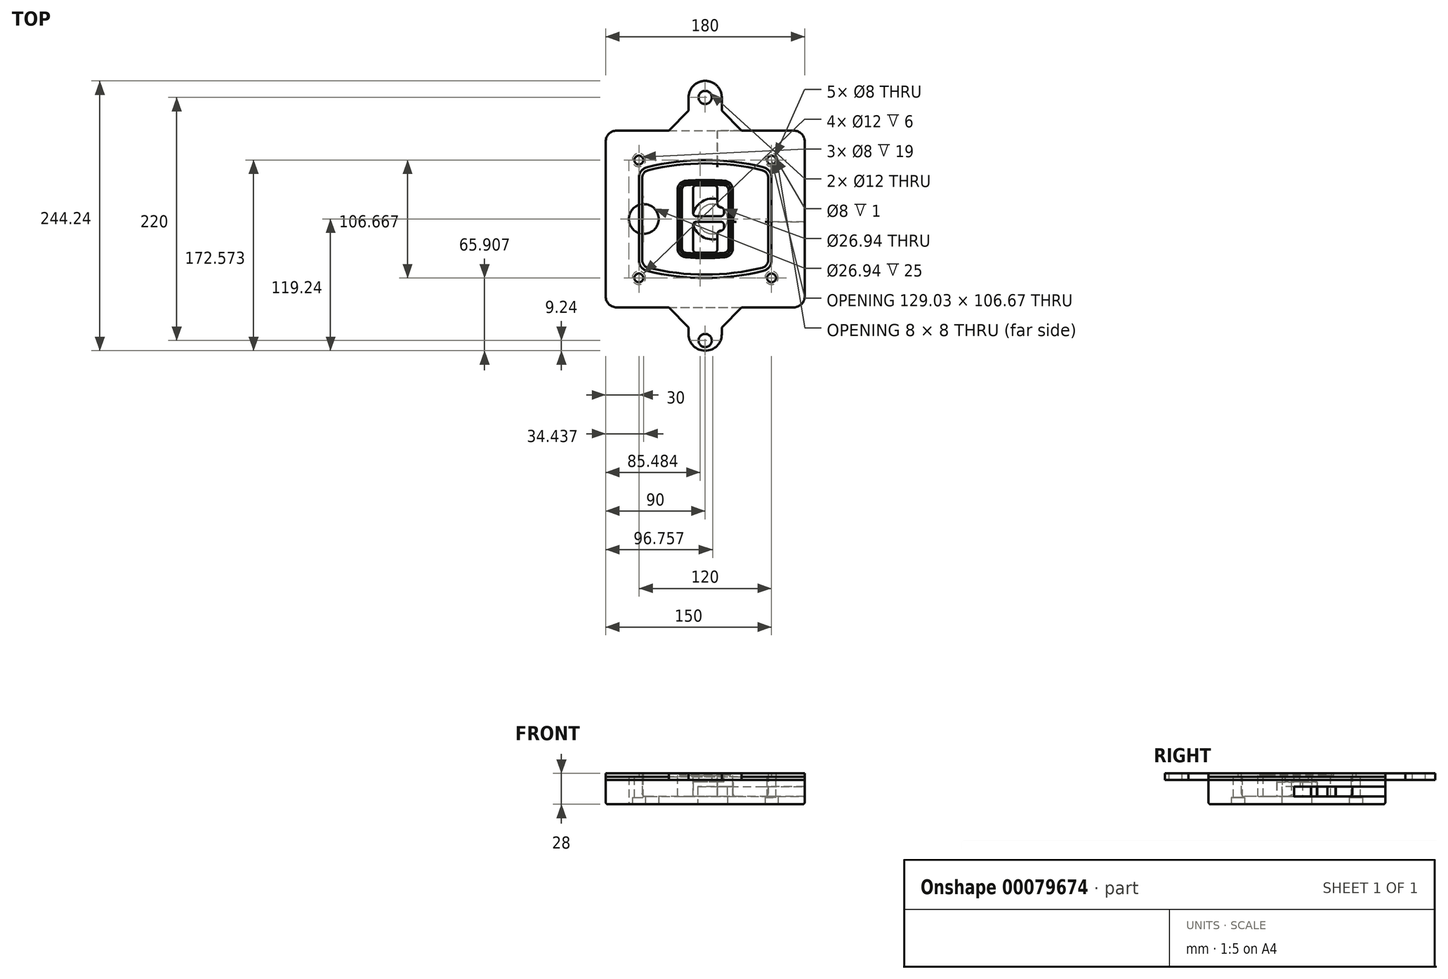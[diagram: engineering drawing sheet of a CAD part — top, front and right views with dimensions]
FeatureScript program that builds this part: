
annotation { "Feature Type Name" : "Feature", "Feature Type Description" : "" }
export const myFeature = defineFeature(function(context is Context, id is Id, definition is map)
    precondition{}
    {
        {
            var Q0;
            Q0=qCreatedBy(makeId("Top.planeOp"),FACE);
            var sketch = newSketch(context, id + "F0", { "sketchPlane" : qUnion([Q0])});
            skPoint(sketch, "E0.rect.middle", {"position": v(0, 0) * mm});
            skLineSegment(sketch, "E1.bottom", {"start": v(-80, -80) * mm, "end": v(80, -80) * mm});
            skLineSegment(sketch, "E1.top", {"start": v(-80, 80) * mm, "end": v(80, 80) * mm});
            skLineSegment(sketch, "E1.left", {"start": v(-90, -70) * mm, "end": v(-90, 70) * mm});
            skLineSegment(sketch, "E1.right", {"start": v(90, -70) * mm, "end": v(90, 70) * mm});
            skLineSegment(sketch, "E2", {"start": v(-90, 80) * mm, "end": v(90, -80) * mm, "construction": true});
            skLineSegment(sketch, "E3", {"start": v(90, 80) * mm, "end": v(-90, -80) * mm, "construction": true});
            skCircle(sketch, "E4", {"center": v(-60, 53.33) * mm, "radius": 4 * mm});
            skCircle(sketch, "E5", {"center": v(60, 53.33) * mm, "radius": 4 * mm});
            skCircle(sketch, "E6", {"center": v(60, -53.33) * mm, "radius": 4 * mm});
            skCircle(sketch, "E7", {"center": v(-60, -53.33) * mm, "radius": 4 * mm});
            skLineSegment(sketch, "E8", {"start": v(-60, 53.33) * mm, "end": v(60, 53.33) * mm, "construction": true});
            skLineSegment(sketch, "E9", {"start": v(60, 53.33) * mm, "end": v(60, -53.33) * mm, "construction": true});
            skLineSegment(sketch, "E10", {"start": v(60, -53.33) * mm, "end": v(-60, -53.33) * mm, "construction": true});
            skLineSegment(sketch, "E11", {"start": v(-60, -53.33) * mm, "end": v(-60, 53.33) * mm, "construction": true});
            skLineSegment(sketch, "E12", {"start": v(-60, 37.3) * mm, "end": v(-60, -37.3) * mm});
            skLineSegment(sketch, "E13", {"start": v(60, 37.3) * mm, "end": v(60, -37.3) * mm});
            skArc(sketch, "E14", {"start": v(52.38, 47.01) * mm, "mid": v(0, 53.33) * mm, "end": v(-52.38, 47.01) * mm});
            skArc(sketch, "E15", {"start": v(-52.38, -47.01) * mm, "mid": v(0, -53.33) * mm, "end": v(52.38, -47.01) * mm});
            skLineSegment(sketch, "E16", {"start": v(-60, 0) * mm, "end": v(60, 0) * mm, "construction": true});
            skPoint(sketch, "E17.visualSharp", {"position": v(-60, -45) * mm});
            skArc(sketch, "E17.filletArc", {"start": v(-60, -37.3) * mm, "mid": v(-57.87, -43.47) * mm, "end": v(-52.38, -47.01) * mm});
            skPoint(sketch, "E18.visualSharp", {"position": v(-60, 45) * mm});
            skArc(sketch, "E18.filletArc", {"start": v(-52.38, 47.01) * mm, "mid": v(-57.87, 43.47) * mm, "end": v(-60, 37.3) * mm});
            skPoint(sketch, "E19.visualSharp", {"position": v(60, 45) * mm});
            skArc(sketch, "E19.filletArc", {"start": v(60, 37.3) * mm, "mid": v(57.87, 43.47) * mm, "end": v(52.38, 47.01) * mm});
            skPoint(sketch, "E20.visualSharp", {"position": v(60, -45) * mm});
            skArc(sketch, "E20.filletArc", {"start": v(52.38, -47.01) * mm, "mid": v(57.87, -43.47) * mm, "end": v(60, -37.3) * mm});
            skPoint(sketch, "E21.visualSharp", {"position": v(-90, 80) * mm});
            skArc(sketch, "E21.filletArc", {"start": v(-80, 80) * mm, "mid": v(-87.07, 77.07) * mm, "end": v(-90, 70) * mm});
            skPoint(sketch, "E22.visualSharp", {"position": v(90, 80) * mm});
            skArc(sketch, "E22.filletArc", {"start": v(90, 70) * mm, "mid": v(87.07, 77.07) * mm, "end": v(80, 80) * mm});
            skPoint(sketch, "E23.visualSharp", {"position": v(90, -80) * mm});
            skArc(sketch, "E23.filletArc", {"start": v(80, -80) * mm, "mid": v(87.07, -77.07) * mm, "end": v(90, -70) * mm});
            skPoint(sketch, "E24.visualSharp", {"position": v(-90, -80) * mm});
            skArc(sketch, "E24.filletArc", {"start": v(-90, -70) * mm, "mid": v(-87.07, -77.07) * mm, "end": v(-80, -80) * mm});
            skArc(sketch, "E25.0", {"start": v(57, 37.3) * mm, "mid": v(55.5, 41.62) * mm, "end": v(51.67, 44.1) * mm});
            skLineSegment(sketch, "E25.1", {"start": v(57, 37.3) * mm, "end": v(57, -37.3) * mm});
            skArc(sketch, "E25.2", {"start": v(51.67, -44.1) * mm, "mid": v(55.5, -41.62) * mm, "end": v(57, -37.3) * mm});
            skArc(sketch, "E25.3", {"start": v(-51.67, -44.1) * mm, "mid": v(0, -50.33) * mm, "end": v(51.67, -44.1) * mm});
            skArc(sketch, "E25.4", {"start": v(-57, -37.3) * mm, "mid": v(-55.5, -41.62) * mm, "end": v(-51.67, -44.1) * mm});
            skArc(sketch, "E25.5", {"start": v(51.67, 44.1) * mm, "mid": v(0, 50.33) * mm, "end": v(-51.67, 44.1) * mm});
            skLineSegment(sketch, "E25.6", {"start": v(-57, 37.3) * mm, "end": v(-57, -37.3) * mm});
            skArc(sketch, "E25.7", {"start": v(-51.67, 44.1) * mm, "mid": v(-55.5, 41.62) * mm, "end": v(-57, 37.3) * mm});
            skArc(sketch, "E26.0", {"start": v(-53.33, 50.9) * mm, "mid": v(-61.01, 45.94) * mm, "end": v(-64, 37.3) * mm});
            skArc(sketch, "E26.1", {"start": v(53.33, 50.9) * mm, "mid": v(0, 57.33) * mm, "end": v(-53.33, 50.9) * mm});
            skArc(sketch, "E26.2", {"start": v(64, 37.3) * mm, "mid": v(61.01, 45.94) * mm, "end": v(53.33, 50.9) * mm});
            skLineSegment(sketch, "E26.3", {"start": v(64, 37.3) * mm, "end": v(64, -37.3) * mm});
            skArc(sketch, "E26.4", {"start": v(53.33, -50.9) * mm, "mid": v(61.01, -45.94) * mm, "end": v(64, -37.3) * mm});
            skLineSegment(sketch, "E26.5", {"start": v(-64, 37.3) * mm, "end": v(-64, -37.3) * mm});
            skArc(sketch, "E26.6", {"start": v(-53.33, -50.9) * mm, "mid": v(0, -57.33) * mm, "end": v(53.33, -50.9) * mm});
            skArc(sketch, "E26.7", {"start": v(-64, -37.3) * mm, "mid": v(-61.01, -45.94) * mm, "end": v(-53.33, -50.9) * mm});
            skSolve(sketch);
        }
        {
            var Q0;
            Q0=makeQuery(id+"F0.imprint","IMPRINT",FACE,{"disambiguationData":[TD([[makeQuery(id+"F0.imprint","IMPRINT",EDGE,{"derivedFrom":sQuery(id+"F0.wireOp",EDGE,"E1.bottom")}),1.0]])]});
            var Q1;
            Q1=makeQuery(id+"F0.imprint","IMPRINT",FACE,{"disambiguationData":[TD([[makeQuery(id+"F0.imprint","IMPRINT",EDGE,{"derivedFrom":sQuery(id+"F0.wireOp",EDGE,"E12")}),1.0]])]});
            var Q2;
            Q2=makeQuery(id+"F0.imprint","IMPRINT",FACE,{"disambiguationData":[TD([[makeQuery(id+"F0.imprint","IMPRINT",EDGE,{"derivedFrom":sQuery(id+"F0.wireOp",EDGE,"E25.0")}),1.0]])]});
            var Q3;
            Q3=makeQuery(id+"F0.imprint","IMPRINT",FACE,{"disambiguationData":[TD([[makeQuery(id+"F0.imprint","IMPRINT",EDGE,{"derivedFrom":sQuery(id+"F0.wireOp",EDGE,"E12")}),-1.0]])]});
            extrude(context, id + "F1", {"entities" : qUnion([Q0, Q1, Q2, Q3]), "oppositeDirection" : true, "depth" : 25 * mm});
        }
        {
            var Q0;
            Q0=makeQuery(id+"F0.imprint","IMPRINT",FACE,{"disambiguationData":[TD([[makeQuery(id+"F0.imprint","IMPRINT",EDGE,{"derivedFrom":sQuery(id+"F0.wireOp",EDGE,"E12")}),1.0]])]});
            extrude(context, id + "F2", {"entities" : qUnion([Q0]), "operationType" : NewBodyOperationType.ADD, "depth" : 3 * mm});
        }
        {
            var Q0;
            Q0=makeQuery(id+"F0.imprint","IMPRINT",FACE,{"disambiguationData":[TD([[makeQuery(id+"F0.imprint","IMPRINT",EDGE,{"derivedFrom":sQuery(id+"F0.wireOp",EDGE,"E25.0")}),1.0]])]});
            extrude(context, id + "F3", {"entities" : qUnion([Q0]), "operationType" : NewBodyOperationType.REMOVE, "oppositeDirection" : true, "depth" : 18 * mm});
        }
        {
            var Q0;
            Q0=makeQuery(id+"F2.opExtrude","CAP_FACE",FACE,{"disambiguationData":[OSD([sQuery(id+"F0.wireOp",EDGE,"E12"),sQuery(id+"F0.wireOp",EDGE,"E13"),sQuery(id+"F0.wireOp",EDGE,"E14"),sQuery(id+"F0.wireOp",EDGE,"E15"),sQuery(id+"F0.wireOp",EDGE,"E17.filletArc"),sQuery(id+"F0.wireOp",EDGE,"E18.filletArc"),sQuery(id+"F0.wireOp",EDGE,"E19.filletArc"),sQuery(id+"F0.wireOp",EDGE,"E20.filletArc"),sQuery(id+"F0.wireOp",EDGE,"E25.0"),sQuery(id+"F0.wireOp",EDGE,"E25.1"),sQuery(id+"F0.wireOp",EDGE,"E25.2"),sQuery(id+"F0.wireOp",EDGE,"E25.3"),sQuery(id+"F0.wireOp",EDGE,"E25.4"),sQuery(id+"F0.wireOp",EDGE,"E25.5"),sQuery(id+"F0.wireOp",EDGE,"E25.6"),sQuery(id+"F0.wireOp",EDGE,"E25.7")])],"isStart":false});
            var sketch = newSketch(context, id + "F4", { "sketchPlane" : qUnion([Q0])});
            skArc(sketch, "E27.0", {"start": v(-17.7, -34.56) * mm, "mid": v(0, -35.33) * mm, "end": v(17.7, -34.56) * mm});
            skArc(sketch, "E28.0", {"start": v(17.7, 34.56) * mm, "mid": v(0, 35.33) * mm, "end": v(-17.7, 34.56) * mm});
            skLineSegment(sketch, "E29", {"start": v(-25, 26.59) * mm, "end": v(-25, -26.59) * mm});
            skLineSegment(sketch, "E30", {"start": v(25, 26.59) * mm, "end": v(25, -26.59) * mm});
            skLineSegment(sketch, "E31", {"start": v(-25, 33.78) * mm, "end": v(25, 33.78) * mm, "construction": true});
            skLineSegment(sketch, "E32", {"start": v(-25, -33.78) * mm, "end": v(25, -33.78) * mm, "construction": true});
            skPoint(sketch, "E33.visualSharp", {"position": v(-25, 33.78) * mm});
            skArc(sketch, "E33.filletArc", {"start": v(-17.7, 34.56) * mm, "mid": v(-22.9, 32) * mm, "end": v(-25, 26.59) * mm});
            skPoint(sketch, "E34.visualSharp", {"position": v(25, 33.78) * mm});
            skArc(sketch, "E34.filletArc", {"start": v(25, 26.59) * mm, "mid": v(22.9, 32) * mm, "end": v(17.7, 34.56) * mm});
            skPoint(sketch, "E35.visualSharp", {"position": v(25, -33.78) * mm});
            skArc(sketch, "E35.filletArc", {"start": v(17.7, -34.56) * mm, "mid": v(22.9, -32) * mm, "end": v(25, -26.59) * mm});
            skPoint(sketch, "E36.visualSharp", {"position": v(-25, -33.78) * mm});
            skArc(sketch, "E36.filletArc", {"start": v(-25, -26.59) * mm, "mid": v(-22.9, -32) * mm, "end": v(-17.7, -34.56) * mm});
            skArc(sketch, "E37.0", {"start": v(51.67, 44.1) * mm, "mid": v(0, 50.33) * mm, "end": v(-51.67, 44.1) * mm});
            skArc(sketch, "E37.1", {"start": v(-51.67, 44.1) * mm, "mid": v(-55.5, 41.62) * mm, "end": v(-57, 37.3) * mm});
            skLineSegment(sketch, "E37.2", {"start": v(-57, 37.3) * mm, "end": v(-57, -37.3) * mm});
            skArc(sketch, "E37.3", {"start": v(-57, -37.3) * mm, "mid": v(-55.5, -41.62) * mm, "end": v(-51.67, -44.1) * mm});
            skArc(sketch, "E37.4", {"start": v(-51.67, -44.1) * mm, "mid": v(0, -50.33) * mm, "end": v(51.67, -44.1) * mm});
            skArc(sketch, "E37.5", {"start": v(51.67, -44.1) * mm, "mid": v(55.5, -41.62) * mm, "end": v(57, -37.3) * mm});
            skLineSegment(sketch, "E37.6", {"start": v(57, 37.3) * mm, "end": v(57, -37.3) * mm});
            skArc(sketch, "E37.7", {"start": v(57, 37.3) * mm, "mid": v(55.5, 41.62) * mm, "end": v(51.67, 44.1) * mm});
            skLineSegment(sketch, "E38.0", {"start": v(23, 26.59) * mm, "end": v(23, -26.59) * mm});
            skArc(sketch, "E38.1", {"start": v(17.53, -32.56) * mm, "mid": v(21.42, -30.64) * mm, "end": v(23, -26.59) * mm});
            skArc(sketch, "E38.2", {"start": v(-17.53, -32.56) * mm, "mid": v(0, -33.33) * mm, "end": v(17.53, -32.56) * mm});
            skArc(sketch, "E38.3", {"start": v(-23, -26.59) * mm, "mid": v(-21.42, -30.64) * mm, "end": v(-17.53, -32.56) * mm});
            skLineSegment(sketch, "E38.4", {"start": v(-23, 26.59) * mm, "end": v(-23, -26.59) * mm});
            skArc(sketch, "E38.5", {"start": v(23, 26.59) * mm, "mid": v(21.42, 30.64) * mm, "end": v(17.53, 32.56) * mm});
            skArc(sketch, "E38.6", {"start": v(-17.53, 32.56) * mm, "mid": v(-21.42, 30.64) * mm, "end": v(-23, 26.59) * mm});
            skArc(sketch, "E38.7", {"start": v(17.53, 32.56) * mm, "mid": v(0, 33.33) * mm, "end": v(-17.53, 32.56) * mm});
            skArc(sketch, "E39.0", {"start": v(21, 26.59) * mm, "mid": v(19.95, 29.29) * mm, "end": v(17.35, 30.57) * mm});
            skLineSegment(sketch, "E39.1", {"start": v(21, 26.59) * mm, "end": v(21, -26.59) * mm});
            skArc(sketch, "E39.2", {"start": v(17.35, -30.57) * mm, "mid": v(19.95, -29.29) * mm, "end": v(21, -26.59) * mm});
            skArc(sketch, "E39.3", {"start": v(-17.35, -30.57) * mm, "mid": v(0, -31.33) * mm, "end": v(17.35, -30.57) * mm});
            skArc(sketch, "E39.4", {"start": v(-21, -26.59) * mm, "mid": v(-19.95, -29.29) * mm, "end": v(-17.35, -30.57) * mm});
            skArc(sketch, "E39.5", {"start": v(17.35, 30.57) * mm, "mid": v(0, 31.33) * mm, "end": v(-17.35, 30.57) * mm});
            skLineSegment(sketch, "E39.6", {"start": v(-21, 26.59) * mm, "end": v(-21, -26.59) * mm});
            skArc(sketch, "E39.7", {"start": v(-17.35, 30.57) * mm, "mid": v(-19.95, 29.29) * mm, "end": v(-21, 26.59) * mm});
            skLineSegment(sketch, "E40", {"start": v(-25, 0) * mm, "end": v(25, 0) * mm, "construction": true});
            skLineSegment(sketch, "E41", {"start": v(-11, 5.5) * mm, "end": v(-11, 27.5) * mm});
            skLineSegment(sketch, "E42", {"start": v(-8, 30.5) * mm, "end": v(8, 30.5) * mm});
            skLineSegment(sketch, "E43", {"start": v(11, 27.5) * mm, "end": v(11, 13.5) * mm});
            skLineSegment(sketch, "E44", {"start": v(14, 10.5) * mm, "end": v(14, 10.5) * mm});
            skLineSegment(sketch, "E45", {"start": v(17, 7.5) * mm, "end": v(17, 5.5) * mm});
            skLineSegment(sketch, "E46", {"start": v(14, 2.5) * mm, "end": v(-8, 2.5) * mm});
            skPoint(sketch, "E47.visualSharp", {"position": v(-11, 30.5) * mm});
            skArc(sketch, "E47.filletArc", {"start": v(-8, 30.5) * mm, "mid": v(-10.12, 29.62) * mm, "end": v(-11, 27.5) * mm});
            skPoint(sketch, "E48.visualSharp", {"position": v(11, 30.5) * mm});
            skArc(sketch, "E48.filletArc", {"start": v(11, 27.5) * mm, "mid": v(10.12, 29.62) * mm, "end": v(8, 30.5) * mm});
            skPoint(sketch, "E49.visualSharp", {"position": v(11, 10.5) * mm});
            skArc(sketch, "E49.filletArc", {"start": v(11, 13.5) * mm, "mid": v(11.88, 11.38) * mm, "end": v(14, 10.5) * mm});
            skPoint(sketch, "E50.visualSharp", {"position": v(17, 10.5) * mm});
            skArc(sketch, "E50.filletArc", {"start": v(17, 7.5) * mm, "mid": v(16.12, 9.62) * mm, "end": v(14, 10.5) * mm});
            skPoint(sketch, "E51.visualSharp", {"position": v(17, 2.5) * mm});
            skArc(sketch, "E51.filletArc", {"start": v(14, 2.5) * mm, "mid": v(16.12, 3.38) * mm, "end": v(17, 5.5) * mm});
            skPoint(sketch, "E52.visualSharp", {"position": v(-11, 2.5) * mm});
            skArc(sketch, "E52.filletArc", {"start": v(-11, 5.5) * mm, "mid": v(-10.12, 3.38) * mm, "end": v(-8, 2.5) * mm});
            skLineSegment(sketch, "E53.0.MirrorCS", {"start": v(14, -2.5) * mm, "end": v(-8, -2.5) * mm});
            skArc(sketch, "E54.0.MirrorCS", {"start": v(-11, -5.5) * mm, "mid": v(-10.12, -3.38) * mm, "end": v(-8, -2.5) * mm});
            skLineSegment(sketch, "E55.0.MirrorCS", {"start": v(-11, -5.5) * mm, "end": v(-11, -27.5) * mm});
            skArc(sketch, "E56.0.MirrorCS", {"start": v(-8, -30.5) * mm, "mid": v(-10.12, -29.62) * mm, "end": v(-11, -27.5) * mm});
            skLineSegment(sketch, "E57.0.MirrorCS", {"start": v(-8, -30.5) * mm, "end": v(8, -30.5) * mm});
            skArc(sketch, "E58.0.MirrorCS", {"start": v(11, -27.5) * mm, "mid": v(10.12, -29.62) * mm, "end": v(8, -30.5) * mm});
            skLineSegment(sketch, "E59.0.MirrorCS", {"start": v(11, -27.5) * mm, "end": v(11, -13.5) * mm});
            skArc(sketch, "E60.0.MirrorCS", {"start": v(11, -13.5) * mm, "mid": v(11.88, -11.38) * mm, "end": v(14, -10.5) * mm});
            skArc(sketch, "E61.0.MirrorCS", {"start": v(17, -7.5) * mm, "mid": v(16.12, -9.62) * mm, "end": v(14, -10.5) * mm});
            skLineSegment(sketch, "E62.0.MirrorCS", {"start": v(17, -7.5) * mm, "end": v(17, -5.5) * mm});
            skArc(sketch, "E63.0.MirrorCS", {"start": v(14, -2.5) * mm, "mid": v(16.12, -3.38) * mm, "end": v(17, -5.5) * mm});
            skSolve(sketch);
        }
        {
            var Q0;
            Q0=makeQuery(id+"F4.imprint","IMPRINT",FACE,{"disambiguationData":[TD([[makeQuery(id+"F4.imprint","IMPRINT",EDGE,{"derivedFrom":sQuery(id+"F4.wireOp",EDGE,"E27.0")}),1.0]])]});
            var Q1;
            Q1=makeQuery(id+"F4.imprint","IMPRINT",FACE,{"disambiguationData":[TD([[makeQuery(id+"F4.imprint","IMPRINT",EDGE,{"derivedFrom":sQuery(id+"F4.wireOp",EDGE,"E38.0")}),-1.0]])]});
            var Q2;
            Q2=makeQuery(id+"F4.imprint","IMPRINT",FACE,{"disambiguationData":[TD([[makeQuery(id+"F4.imprint","IMPRINT",EDGE,{"derivedFrom":sQuery(id+"F4.wireOp",EDGE,"E39.0")}),1.0]])]});
            extrude(context, id + "F5", {"entities" : qUnion([Q0, Q1, Q2]), "operationType" : NewBodyOperationType.ADD, "endBound" : BoundingType.UP_TO_NEXT, "oppositeDirection" : true, "depth" : 25 * mm});
        }
        {
            var Q0;
            Q0=makeQuery(id+"F4.imprint","IMPRINT",FACE,{"disambiguationData":[TD([[makeQuery(id+"F4.imprint","IMPRINT",EDGE,{"derivedFrom":sQuery(id+"F4.wireOp",EDGE,"E38.0")}),-1.0]])]});
            extrude(context, id + "F6", {"entities" : qUnion([Q0]), "operationType" : NewBodyOperationType.REMOVE, "oppositeDirection" : true, "depth" : 2 * mm});
        }
        {
            var Q0;
            Q0=makeQuery(id+"F1.opExtrude","CAP_FACE",FACE,{"disambiguationData":[OSD([sQuery(id+"F0.wireOp",EDGE,"E1.bottom"),sQuery(id+"F0.wireOp",EDGE,"E1.top"),sQuery(id+"F0.wireOp",EDGE,"E1.left"),sQuery(id+"F0.wireOp",EDGE,"E1.right"),sQuery(id+"F0.wireOp",EDGE,"E4"),sQuery(id+"F0.wireOp",EDGE,"E5"),sQuery(id+"F0.wireOp",EDGE,"E6"),sQuery(id+"F0.wireOp",EDGE,"E7"),sQuery(id+"F0.wireOp",EDGE,"E21.filletArc"),sQuery(id+"F0.wireOp",EDGE,"E22.filletArc"),sQuery(id+"F0.wireOp",EDGE,"E23.filletArc"),sQuery(id+"F0.wireOp",EDGE,"E24.filletArc")])],"isStart":false});
            var sketch = newSketch(context, id + "F7", { "sketchPlane" : qUnion([Q0])});
            skCircle(sketch, "E64", {"center": v(6.76, 0) * mm, "radius": 13.47 * mm});
            skCircle(sketch, "E65", {"center": v(-55.56, 0) * mm, "radius": 13.47 * mm});
            skLineSegment(sketch, "E66", {"start": v(90, 0) * mm, "end": v(-90, 0) * mm});
            skCircle(sketch, "E67", {"center": v(6.76, 0) * mm, "radius": 18.47 * mm});
            skCircle(sketch, "E68", {"center": v(60, -53.33) * mm, "radius": 6 * mm});
            skCircle(sketch, "E69", {"center": v(-60, -53.33) * mm, "radius": 6 * mm});
            skCircle(sketch, "E70", {"center": v(-60, 53.33) * mm, "radius": 6 * mm});
            skCircle(sketch, "E71", {"center": v(60, 53.33) * mm, "radius": 6 * mm});
            skSolve(sketch);
        }
        {
            var Q0;
            {var subQ1=sQuery(id+"F7.wireOp",EDGE,"E66");var subQ4=sQuery(id+"F7.wireOp",EDGE,"E64");var subQ6=makeQuery(id+"F7.imprint","INTERSECT",VERTEX,{"disambiguationData":[OD(0.0)],"derivedFrom":[subQ4,subQ1]});Q0=makeQuery(id+"F7.imprint","IMPRINT",FACE,{"disambiguationData":[TD([[makeQuery(id+"F7.imprint","IMPRINT",EDGE,{"disambiguationData":[TD([[subQ6,-1.0]])],"derivedFrom":subQ4}),-1.0]])]});}
            var Q1;
            {var subQ0=sQuery(id+"F7.wireOp",EDGE,"E66");var subQ1=sQuery(id+"F7.wireOp",EDGE,"E64");var subQ3=makeQuery(id+"F7.imprint","INTERSECT",VERTEX,{"disambiguationData":[OD(0.0)],"derivedFrom":[subQ1,subQ0]});Q1=makeQuery(id+"F7.imprint","IMPRINT",FACE,{"disambiguationData":[TD([[makeQuery(id+"F7.imprint","IMPRINT",EDGE,{"disambiguationData":[TD([[subQ3,-1.0]])],"derivedFrom":subQ1}),1.0]])]});}
            var Q2;
            {var subQ0=sQuery(id+"F7.wireOp",EDGE,"E66");var subQ1=sQuery(id+"F7.wireOp",EDGE,"E64");var subQ3=makeQuery(id+"F7.imprint","INTERSECT",VERTEX,{"disambiguationData":[OD(0.0)],"derivedFrom":[subQ1,subQ0]});Q2=makeQuery(id+"F7.imprint","IMPRINT",FACE,{"disambiguationData":[TD([[makeQuery(id+"F7.imprint","IMPRINT",EDGE,{"disambiguationData":[TD([[subQ3,1.0]])],"derivedFrom":subQ1}),1.0]])]});}
            var Q3;
            {var subQ1=sQuery(id+"F7.wireOp",EDGE,"E66");var subQ4=sQuery(id+"F7.wireOp",EDGE,"E64");var subQ6=makeQuery(id+"F7.imprint","INTERSECT",VERTEX,{"disambiguationData":[OD(0.0)],"derivedFrom":[subQ4,subQ1]});Q3=makeQuery(id+"F7.imprint","IMPRINT",FACE,{"disambiguationData":[TD([[makeQuery(id+"F7.imprint","IMPRINT",EDGE,{"disambiguationData":[TD([[subQ6,1.0]])],"derivedFrom":subQ4}),-1.0]])]});}
            extrude(context, id + "F8", {"entities" : qUnion([Q0, Q1, Q2, Q3]), "operationType" : NewBodyOperationType.ADD, "oppositeDirection" : true, "depth" : 20 * mm});
        }
        {
            var Q0;
            {var subQ0=sQuery(id+"F7.wireOp",EDGE,"E66");var subQ1=sQuery(id+"F7.wireOp",EDGE,"E64");var subQ3=makeQuery(id+"F7.imprint","INTERSECT",VERTEX,{"disambiguationData":[OD(0.0)],"derivedFrom":[subQ1,subQ0]});Q0=makeQuery(id+"F7.imprint","IMPRINT",FACE,{"disambiguationData":[TD([[makeQuery(id+"F7.imprint","IMPRINT",EDGE,{"disambiguationData":[TD([[subQ3,-1.0]])],"derivedFrom":subQ1}),1.0]])]});}
            var Q1;
            {var subQ0=sQuery(id+"F7.wireOp",EDGE,"E66");var subQ1=sQuery(id+"F7.wireOp",EDGE,"E64");var subQ3=makeQuery(id+"F7.imprint","INTERSECT",VERTEX,{"disambiguationData":[OD(0.0)],"derivedFrom":[subQ1,subQ0]});Q1=makeQuery(id+"F7.imprint","IMPRINT",FACE,{"disambiguationData":[TD([[makeQuery(id+"F7.imprint","IMPRINT",EDGE,{"disambiguationData":[TD([[subQ3,1.0]])],"derivedFrom":subQ1}),1.0]])]});}
            extrude(context, id + "F9", {"entities" : qUnion([Q0, Q1]), "operationType" : NewBodyOperationType.REMOVE, "oppositeDirection" : true, "depth" : 16 * mm});
        }
        {
            var Q0;
            {var subQ0=sQuery(id+"F7.wireOp",EDGE,"E66");var subQ1=sQuery(id+"F7.wireOp",EDGE,"E65");var subQ3=makeQuery(id+"F7.imprint","INTERSECT",VERTEX,{"disambiguationData":[OD(0.0)],"derivedFrom":[subQ1,subQ0]});Q0=makeQuery(id+"F7.imprint","IMPRINT",FACE,{"disambiguationData":[TD([[makeQuery(id+"F7.imprint","IMPRINT",EDGE,{"disambiguationData":[TD([[subQ3,-1.0]])],"derivedFrom":subQ1}),1.0]])]});}
            var Q1;
            {var subQ0=sQuery(id+"F7.wireOp",EDGE,"E66");var subQ1=sQuery(id+"F7.wireOp",EDGE,"E65");var subQ3=makeQuery(id+"F7.imprint","INTERSECT",VERTEX,{"disambiguationData":[OD(0.0)],"derivedFrom":[subQ1,subQ0]});Q1=makeQuery(id+"F7.imprint","IMPRINT",FACE,{"disambiguationData":[TD([[makeQuery(id+"F7.imprint","IMPRINT",EDGE,{"disambiguationData":[TD([[subQ3,1.0]])],"derivedFrom":subQ1}),1.0]])]});}
            extrude(context, id + "F10", {"entities" : qUnion([Q0, Q1]), "operationType" : NewBodyOperationType.REMOVE, "oppositeDirection" : true, "depth" : 25 * mm});
        }
        {
            var Q0;
            Q0=makeQuery(id+"F7.imprint","IMPRINT",FACE,{"disambiguationData":[TD([[makeQuery(id+"F7.imprint","IMPRINT",EDGE,{"derivedFrom":sQuery(id+"F7.wireOp",EDGE,"E68")}),1.0]])]});
            var Q1;
            Q1=makeQuery(id+"F7.imprint","IMPRINT",FACE,{"disambiguationData":[TD([[makeQuery(id+"F7.imprint","IMPRINT",EDGE,{"derivedFrom":makeQuery(id+"F1.opExtrude","CAP_EDGE",EDGE,{"disambiguationData":[OSD([sQuery(id+"F0.wireOp",EDGE,"E5")])],"isStart":false})}),-1.0]])]});
            var Q2;
            Q2=makeQuery(id+"F7.imprint","IMPRINT",FACE,{"disambiguationData":[TD([[makeQuery(id+"F7.imprint","IMPRINT",EDGE,{"derivedFrom":sQuery(id+"F7.wireOp",EDGE,"E69")}),1.0]])]});
            var Q3;
            Q3=makeQuery(id+"F7.imprint","IMPRINT",FACE,{"disambiguationData":[TD([[makeQuery(id+"F7.imprint","IMPRINT",EDGE,{"derivedFrom":makeQuery(id+"F1.opExtrude","CAP_EDGE",EDGE,{"disambiguationData":[OSD([sQuery(id+"F0.wireOp",EDGE,"E4")])],"isStart":false})}),-1.0]])]});
            var Q4;
            Q4=makeQuery(id+"F7.imprint","IMPRINT",FACE,{"disambiguationData":[TD([[makeQuery(id+"F7.imprint","IMPRINT",EDGE,{"derivedFrom":sQuery(id+"F7.wireOp",EDGE,"E70")}),1.0]])]});
            var Q5;
            Q5=makeQuery(id+"F7.imprint","IMPRINT",FACE,{"disambiguationData":[TD([[makeQuery(id+"F7.imprint","IMPRINT",EDGE,{"derivedFrom":makeQuery(id+"F1.opExtrude","CAP_EDGE",EDGE,{"disambiguationData":[OSD([sQuery(id+"F0.wireOp",EDGE,"E7")])],"isStart":false})}),-1.0]])]});
            var Q6;
            Q6=makeQuery(id+"F7.imprint","IMPRINT",FACE,{"disambiguationData":[TD([[makeQuery(id+"F7.imprint","IMPRINT",EDGE,{"derivedFrom":sQuery(id+"F7.wireOp",EDGE,"E71")}),1.0]])]});
            var Q7;
            Q7=makeQuery(id+"F7.imprint","IMPRINT",FACE,{"disambiguationData":[TD([[makeQuery(id+"F7.imprint","IMPRINT",EDGE,{"derivedFrom":makeQuery(id+"F1.opExtrude","CAP_EDGE",EDGE,{"disambiguationData":[OSD([sQuery(id+"F0.wireOp",EDGE,"E6")])],"isStart":false})}),-1.0]])]});
            extrude(context, id + "F11", {"entities" : qUnion([Q0, Q1, Q2, Q3, Q4, Q5, Q6, Q7]), "operationType" : NewBodyOperationType.REMOVE, "oppositeDirection" : true, "depth" : 6 * mm});
        }
        {
            var Q0;
            Q0=makeQuery(id+"F9.boolean.opBoolean","COPY",FACE,{"derivedFrom":makeQuery(id+"F9.opExtrude","CAP_FACE",FACE,{"disambiguationData":[OSD([sQuery(id+"F7.wireOp",EDGE,"E64")])],"isStart":false})});
            var sketch = newSketch(context, id + "F12", { "sketchPlane" : qUnion([Q0])});
            skArc(sketch, "E72.0", {"start": v(11, -88.19) * mm, "mid": v(97.1, -83.6) * mm, "end": v(92.5, 2.5) * mm});
            skLineSegment(sketch, "E72.1", {"start": v(11, -17.97) * mm, "end": v(11, -17.97) * mm});
            skLineSegment(sketch, "E73", {"start": v(92.5, -105.13) * mm, "end": v(102.3, -105.13) * mm});
            skLineSegment(sketch, "E74.0", {"start": v(92.5, 2.5) * mm, "end": v(14, 2.5) * mm});
            skArc(sketch, "E74.1", {"start": v(14, 2.5) * mm, "mid": v(16.12, 3.38) * mm, "end": v(17, 5.5) * mm});
            skLineSegment(sketch, "E74.2", {"start": v(17, 7.5) * mm, "end": v(17, 5.5) * mm});
            skArc(sketch, "E74.3", {"start": v(17, 7.5) * mm, "mid": v(16.12, 9.62) * mm, "end": v(14, 10.5) * mm});
            skArc(sketch, "E74.4", {"start": v(11, 13.5) * mm, "mid": v(11.88, 11.38) * mm, "end": v(14, 10.5) * mm});
            skLineSegment(sketch, "E74.5", {"start": v(11, 13.5) * mm, "end": v(11, -88.19) * mm});
            skLineSegment(sketch, "E74.7", {"start": v(92.5, -2.5) * mm, "end": v(14, -2.5) * mm});
            skArc(sketch, "E74.8", {"start": v(14, -2.5) * mm, "mid": v(16.12, -3.38) * mm, "end": v(17, -5.5) * mm});
            skLineSegment(sketch, "E74.9", {"start": v(17, -7.5) * mm, "end": v(17, -5.5) * mm});
            skArc(sketch, "E74.10", {"start": v(17, -7.5) * mm, "mid": v(16.12, -9.62) * mm, "end": v(14, -10.5) * mm});
            skArc(sketch, "E74.11", {"start": v(11, -13.5) * mm, "mid": v(11.88, -11.38) * mm, "end": v(14, -10.5) * mm});
            skLineSegment(sketch, "E74.12", {"start": v(11, -17.97) * mm, "end": v(11, -13.5) * mm});
            skPoint(sketch, "E75.orphan", {"position": v(11, -27.5) * mm});
            skPoint(sketch, "E76.orphan", {"position": v(-8, -2.5) * mm});
            skPoint(sketch, "E77.orphan", {"position": v(-8, 2.5) * mm});
            skPoint(sketch, "E78.orphan", {"position": v(11, 27.5) * mm});
            skSolve(sketch);
        }
        {
            var Q0;
            {var subQ7=sQuery(id+"F12.wireOp",EDGE,"E72.0");var subQ14=sQuery(id+"F12.wireOp",EDGE,"E72.1");var subQ16=sQuery(id+"F12.wireOp",EDGE,"E74.1");var subQ18=sQuery(id+"F12.wireOp",EDGE,"E74.8");Q0=qUnion([makeQuery(id+"F12.imprint","IMPRINT",FACE,{"disambiguationData":[TD([[makeQuery(id+"F12.imprint","IMPRINT",EDGE,{"derivedFrom":subQ7}),1.0]])]}),makeQuery(id+"F12.imprint","IMPRINT",FACE,{"disambiguationData":[TD([[makeQuery(id+"F12.imprint","IMPRINT",EDGE,{"derivedFrom":subQ14}),1.0]])]}),makeQuery(id+"F12.imprint","IMPRINT",FACE,{"disambiguationData":[TD([[makeQuery(id+"F12.imprint","IMPRINT",EDGE,{"derivedFrom":subQ16}),1.0]])]}),makeQuery(id+"F12.imprint","IMPRINT",FACE,{"disambiguationData":[TD([[makeQuery(id+"F12.imprint","IMPRINT",EDGE,{"derivedFrom":subQ18}),-1.0]])]})]);}
            var Q1;
            Q1=makeQuery(id+"F5.boolean.opBoolean","SPLIT",FACE,{"disambiguationData":[TD([makeQuery(id+"F5.opExtrude","SWEPT_FACE",FACE,{"disambiguationData":[OSD([sQuery(id+"F4.wireOp",EDGE,"E41")])]})])],"derivedFrom":makeQuery(id+"F3.boolean.opBoolean","COPY",FACE,{"derivedFrom":makeQuery(id+"F3.opExtrude","CAP_FACE",FACE,{"disambiguationData":[OSD([sQuery(id+"F0.wireOp",EDGE,"E25.0"),sQuery(id+"F0.wireOp",EDGE,"E25.1"),sQuery(id+"F0.wireOp",EDGE,"E25.2"),sQuery(id+"F0.wireOp",EDGE,"E25.3"),sQuery(id+"F0.wireOp",EDGE,"E25.4"),sQuery(id+"F0.wireOp",EDGE,"E25.5"),sQuery(id+"F0.wireOp",EDGE,"E25.6"),sQuery(id+"F0.wireOp",EDGE,"E25.7")])],"isStart":false})})});
            extrude(context, id + "F13", {"entities" : qUnion([Q0]), "operationType" : NewBodyOperationType.REMOVE, "endBound" : BoundingType.UP_TO_SURFACE, "endBoundEntityFace" : qUnion([Q1]), "depth" : 25 * mm});
        }
        {
            var Q0;
            Q0=makeQuery(id+"F3.boolean.opBoolean","COPY",EDGE,{"derivedFrom":makeQuery(id+"F3.opExtrude","CAP_EDGE",EDGE,{"disambiguationData":[OSD([sQuery(id+"F0.wireOp",EDGE,"E25.6")])],"isStart":false})});
            var Q1;
            Q1=makeQuery(id+"F8.boolean.opBoolean","INTERSECT",EDGE,{"derivedFrom":[makeQuery(id+"F5.opExtrude","SWEPT_FACE",FACE,{"disambiguationData":[OSD([sQuery(id+"F4.wireOp",EDGE,"E30")])]}),makeQuery(id+"F8.opExtrude","CAP_FACE",FACE,{"disambiguationData":[OSD([sQuery(id+"F7.wireOp",EDGE,"E67")])],"isStart":false})]});
            var Q2;
            Q2=makeQuery(id+"F8.boolean.opBoolean","INTERSECT",EDGE,{"disambiguationData":[OD(1.0)],"derivedFrom":[makeQuery(id+"F5.opExtrude","SWEPT_FACE",FACE,{"disambiguationData":[OSD([sQuery(id+"F4.wireOp",EDGE,"E30")])]}),makeQuery(id+"F8.opExtrude","SWEPT_FACE",FACE,{"disambiguationData":[OSD([sQuery(id+"F7.wireOp",EDGE,"E67")])]})]});
            var Q3;
            {var subQ0=makeQuery(id+"F3.boolean.opBoolean","COPY",FACE,{"derivedFrom":makeQuery(id+"F3.opExtrude","CAP_FACE",FACE,{"disambiguationData":[OSD([sQuery(id+"F0.wireOp",EDGE,"E25.0"),sQuery(id+"F0.wireOp",EDGE,"E25.1"),sQuery(id+"F0.wireOp",EDGE,"E25.2"),sQuery(id+"F0.wireOp",EDGE,"E25.3"),sQuery(id+"F0.wireOp",EDGE,"E25.4"),sQuery(id+"F0.wireOp",EDGE,"E25.5"),sQuery(id+"F0.wireOp",EDGE,"E25.6"),sQuery(id+"F0.wireOp",EDGE,"E25.7")])],"isStart":false})});var subQ1=sQuery(id+"F4.wireOp",EDGE,"E30");Q3=makeQuery(id+"F8.boolean.opBoolean","SPLIT",EDGE,{"disambiguationData":[TD([makeQuery(id+"F5.opExtrude","SWEPT_FACE",FACE,{"disambiguationData":[OSD([sQuery(id+"F4.wireOp",EDGE,"E35.filletArc")])]})])],"derivedFrom":makeQuery(id+"F5.opExtrude","TWEAK_EDGE",EDGE,{"derivedFrom":[subQ0,makeQuery(id+"F4.imprint","IMPRINT",EDGE,{"derivedFrom":subQ1})]})});}
            var Q4;
            {var subQ0=sQuery(id+"F0.wireOp",EDGE,"E25.0");var subQ1=sQuery(id+"F0.wireOp",EDGE,"E25.1");var subQ2=sQuery(id+"F0.wireOp",EDGE,"E25.2");var subQ3=sQuery(id+"F0.wireOp",EDGE,"E25.3");var subQ4=sQuery(id+"F0.wireOp",EDGE,"E25.4");var subQ5=sQuery(id+"F0.wireOp",EDGE,"E25.5");var subQ6=sQuery(id+"F0.wireOp",EDGE,"E25.6");var subQ7=sQuery(id+"F0.wireOp",EDGE,"E25.7");Q4=makeQuery(id+"F8.boolean.opBoolean","INTERSECT",EDGE,{"derivedFrom":[makeQuery(id+"F5.boolean.opBoolean","SPLIT",FACE,{"disambiguationData":[TD([makeQuery(id+"F2.opExtrude","SWEPT_FACE",FACE,{"disambiguationData":[OSD([subQ0])]})])],"derivedFrom":makeQuery(id+"F3.boolean.opBoolean","COPY",FACE,{"derivedFrom":makeQuery(id+"F3.opExtrude","CAP_FACE",FACE,{"disambiguationData":[OSD([subQ0,subQ1,subQ2,subQ3,subQ4,subQ5,subQ6,subQ7])],"isStart":false})})}),makeQuery(id+"F8.opExtrude","SWEPT_FACE",FACE,{"disambiguationData":[OSD([sQuery(id+"F7.wireOp",EDGE,"E67")])]})]});}
            var Q5;
            Q5=makeQuery(id+"F8.boolean.opBoolean","INTERSECT",EDGE,{"disambiguationData":[OD(0.0)],"derivedFrom":[makeQuery(id+"F5.opExtrude","SWEPT_FACE",FACE,{"disambiguationData":[OSD([sQuery(id+"F4.wireOp",EDGE,"E30")])]}),makeQuery(id+"F8.opExtrude","SWEPT_FACE",FACE,{"disambiguationData":[OSD([sQuery(id+"F7.wireOp",EDGE,"E67")])]})]});
            fillet(context, id + "F14", {"entities" : qUnion([Q0, Q1, Q2, Q3, Q4, Q5]), "radius" : 3 * mm, "tangentPropagation" : true, "allowEdgeOverflow" : false});
        }
        {
            var Q0;
            Q0=makeQuery(id+"F1.opExtrude","CAP_EDGE",EDGE,{"disambiguationData":[OSD([sQuery(id+"F0.wireOp",EDGE,"E1.bottom")])],"isStart":false});
            fillet(context, id + "F15", {"entities" : qUnion([Q0]), "radius" : 2 * mm, "tangentPropagation" : true, "allowEdgeOverflow" : false});
        }
        {
            var Q0;
            {var subQ0=sQuery(id+"F0.wireOp",EDGE,"E22.filletArc");var subQ1=sQuery(id+"F0.wireOp",EDGE,"E7");var subQ2=sQuery(id+"F0.wireOp",EDGE,"E6");var subQ3=sQuery(id+"F0.wireOp",EDGE,"E5");var subQ4=sQuery(id+"F0.wireOp",EDGE,"E4");var subQ5=sQuery(id+"F0.wireOp",EDGE,"E1.bottom");var subQ6=sQuery(id+"F0.wireOp",EDGE,"E21.filletArc");var subQ7=sQuery(id+"F0.wireOp",EDGE,"E1.top");var subQ8=sQuery(id+"F0.wireOp",EDGE,"E1.left");var subQ9=sQuery(id+"F0.wireOp",EDGE,"E1.right");var subQ10=sQuery(id+"F0.wireOp",EDGE,"E23.filletArc");var subQ11=sQuery(id+"F0.wireOp",EDGE,"E24.filletArc");Q0=makeQuery(id+"F2.boolean.opBoolean","SPLIT",FACE,{"disambiguationData":[TD([makeQuery(id+"F1.opExtrude","SWEPT_FACE",FACE,{"disambiguationData":[OSD([subQ5])]})])],"derivedFrom":makeQuery(id+"F1.opExtrude","CAP_FACE",FACE,{"disambiguationData":[OSD([subQ5,subQ7,subQ8,subQ9,subQ4,subQ3,subQ2,subQ1,subQ6,subQ0,subQ10,subQ11])],"isStart":true})});}
            var sketch = newSketch(context, id + "F16", { "sketchPlane" : qUnion([Q0])});
            skLineSegment(sketch, "E79.0", {"start": v(-90, -70) * mm, "end": v(-90, 70) * mm});
            skArc(sketch, "E80.0", {"start": v(-80, 80) * mm, "mid": v(-87.07, 77.07) * mm, "end": v(-90, 70) * mm});
            skLineSegment(sketch, "E81.0", {"start": v(-80, 80) * mm, "end": v(80, 80) * mm});
            skLineSegment(sketch, "E82.0", {"start": v(90, -70) * mm, "end": v(90, 70) * mm});
            skArc(sketch, "E83.0", {"start": v(90, 70) * mm, "mid": v(87.07, 77.07) * mm, "end": v(80, 80) * mm});
            skArc(sketch, "E84.0", {"start": v(80, -80) * mm, "mid": v(87.07, -77.07) * mm, "end": v(90, -70) * mm});
            skLineSegment(sketch, "E85.0", {"start": v(-80, -80) * mm, "end": v(80, -80) * mm});
            skArc(sketch, "E86.0", {"start": v(-90, -70) * mm, "mid": v(-87.07, -77.07) * mm, "end": v(-80, -80) * mm});
            skCircle(sketch, "E87.0", {"center": v(60, 53.33) * mm, "radius": 4 * mm});
            skLineSegment(sketch, "E88.0", {"start": v(60, 37.3) * mm, "end": v(60, -37.3) * mm});
            skCircle(sketch, "E89.0", {"center": v(60, -53.33) * mm, "radius": 4 * mm});
            skCircle(sketch, "E90.0", {"center": v(-60, -53.33) * mm, "radius": 4 * mm});
            skLineSegment(sketch, "E91.0", {"start": v(-60, 37.3) * mm, "end": v(-60, -37.3) * mm});
            skArc(sketch, "E92.0", {"start": v(-52.38, -47.01) * mm, "mid": v(0, -53.33) * mm, "end": v(52.38, -47.01) * mm});
            skArc(sketch, "E93.0", {"start": v(52.38, 47.01) * mm, "mid": v(0, 53.33) * mm, "end": v(-52.38, 47.01) * mm});
            skArc(sketch, "E94.0", {"start": v(52.38, -47.01) * mm, "mid": v(57.87, -43.47) * mm, "end": v(60, -37.3) * mm});
            skArc(sketch, "E95.0", {"start": v(-52.38, 47.01) * mm, "mid": v(-57.87, 43.47) * mm, "end": v(-60, 37.3) * mm});
            skArc(sketch, "E96.0", {"start": v(-60, -37.3) * mm, "mid": v(-57.87, -43.47) * mm, "end": v(-52.38, -47.01) * mm});
            skArc(sketch, "E97.0", {"start": v(60, 37.3) * mm, "mid": v(57.87, 43.47) * mm, "end": v(52.38, 47.01) * mm});
            skLineSegment(sketch, "E98", {"start": v(0, 80) * mm, "end": v(0, 110) * mm, "construction": true});
            skCircle(sketch, "E99", {"center": v(0, 110) * mm, "radius": 6 * mm});
            skLineSegment(sketch, "E100", {"start": v(-33, 80) * mm, "end": v(-15, 98) * mm});
            skLineSegment(sketch, "E101", {"start": v(-15, 98) * mm, "end": v(-15, 110) * mm});
            skLineSegment(sketch, "E102", {"start": v(32.99, 80) * mm, "end": v(15, 97.99) * mm});
            skLineSegment(sketch, "E103", {"start": v(15, 97.99) * mm, "end": v(15, 110) * mm});
            skArc(sketch, "E104", {"start": v(15, 110) * mm, "mid": v(0, 125) * mm, "end": v(-15, 110) * mm});
            skLineSegment(sketch, "E105", {"start": v(-90, 0) * mm, "end": v(90, 0) * mm, "construction": true});
            skLineSegment(sketch, "E106.MirrorCS", {"start": v(33, 80) * mm, "end": v(15, 98) * mm});
            skLineSegment(sketch, "E107.MirrorCS", {"start": v(15, 98) * mm, "end": v(15, 110) * mm});
            skLineSegment(sketch, "E108.MirrorCS", {"start": v(-15, 97.99) * mm, "end": v(-15, 110) * mm});
            skLineSegment(sketch, "E109.MirrorCS", {"start": v(-32.99, 80) * mm, "end": v(-15, 97.99) * mm});
            skArc(sketch, "E110.MirrorCS", {"start": v(-15, 110) * mm, "mid": v(0, 125) * mm, "end": v(15, 110) * mm});
            skLineSegment(sketch, "E111.MirrorCS", {"start": v(90, 0) * mm, "end": v(-90, 0) * mm, "construction": true});
            skLineSegment(sketch, "E112.MirrorCS", {"start": v(80, 80) * mm, "end": v(-80, 80) * mm});
            skLineSegment(sketch, "E113.MirrorCS", {"start": v(32.99, -80) * mm, "end": v(15, -97.99) * mm});
            skLineSegment(sketch, "E114.MirrorCS", {"start": v(-32.99, -80) * mm, "end": v(-15, -97.99) * mm});
            skLineSegment(sketch, "E115", {"start": v(0, -80) * mm, "end": v(0, -110) * mm, "construction": true});
            skCircle(sketch, "E116", {"center": v(0, -110) * mm, "radius": 6 * mm});
            skLineSegment(sketch, "E117", {"start": v(-15, -97.99) * mm, "end": v(-15, -104.24) * mm});
            skLineSegment(sketch, "E118", {"start": v(15, -97.99) * mm, "end": v(15, -104.24) * mm});
            skArc(sketch, "E119", {"start": v(-15, -104.24) * mm, "mid": v(0, -119.24) * mm, "end": v(15, -104.24) * mm});
            skSolve(sketch);
        }
        {
            var Q0;
            Q0=makeQuery(id+"F16.imprint","IMPRINT",FACE,{"disambiguationData":[TD([[makeQuery(id+"F16.imprint","IMPRINT",EDGE,{"derivedFrom":sQuery(id+"F16.wireOp",EDGE,"E79.0")}),-1.0]])]});
            var Q1;
            {var subQ2=sQuery(id+"F16.wireOp",EDGE,"E103");Q1=makeQuery(id+"F16.imprint","IMPRINT",FACE,{"disambiguationData":[TD([[makeQuery(id+"F16.imprint","IMPRINT",EDGE,{"derivedFrom":subQ2}),1.0]])]});}
            var Q2;
            {var subQ2=sQuery(id+"F16.wireOp",EDGE,"E103");Q2=makeQuery(id+"F16.imprint","IMPRINT",FACE,{"disambiguationData":[TD([[makeQuery(id+"F16.imprint","IMPRINT",EDGE,{"derivedFrom":subQ2}),-1.0]])]});}
            var Q3;
            {var subQ4=sQuery(id+"F16.wireOp",EDGE,"E101");Q3=makeQuery(id+"F16.imprint","IMPRINT",FACE,{"disambiguationData":[TD([[makeQuery(id+"F16.imprint","IMPRINT",EDGE,{"derivedFrom":subQ4}),-1.0]])]});}
            var Q4;
            {var subQ1=sQuery(id+"F16.wireOp",EDGE,"E113.MirrorCS");Q4=makeQuery(id+"F16.imprint","IMPRINT",FACE,{"disambiguationData":[TD([[makeQuery(id+"F16.imprint","IMPRINT",EDGE,{"derivedFrom":subQ1}),-1.0]])]});}
            extrude(context, id + "F17", {"entities" : qUnion([Q0, Q1, Q2, Q3, Q4]), "endBound" : BoundingType.SYMMETRIC, "depth" : 6 * mm});
        }
    });
